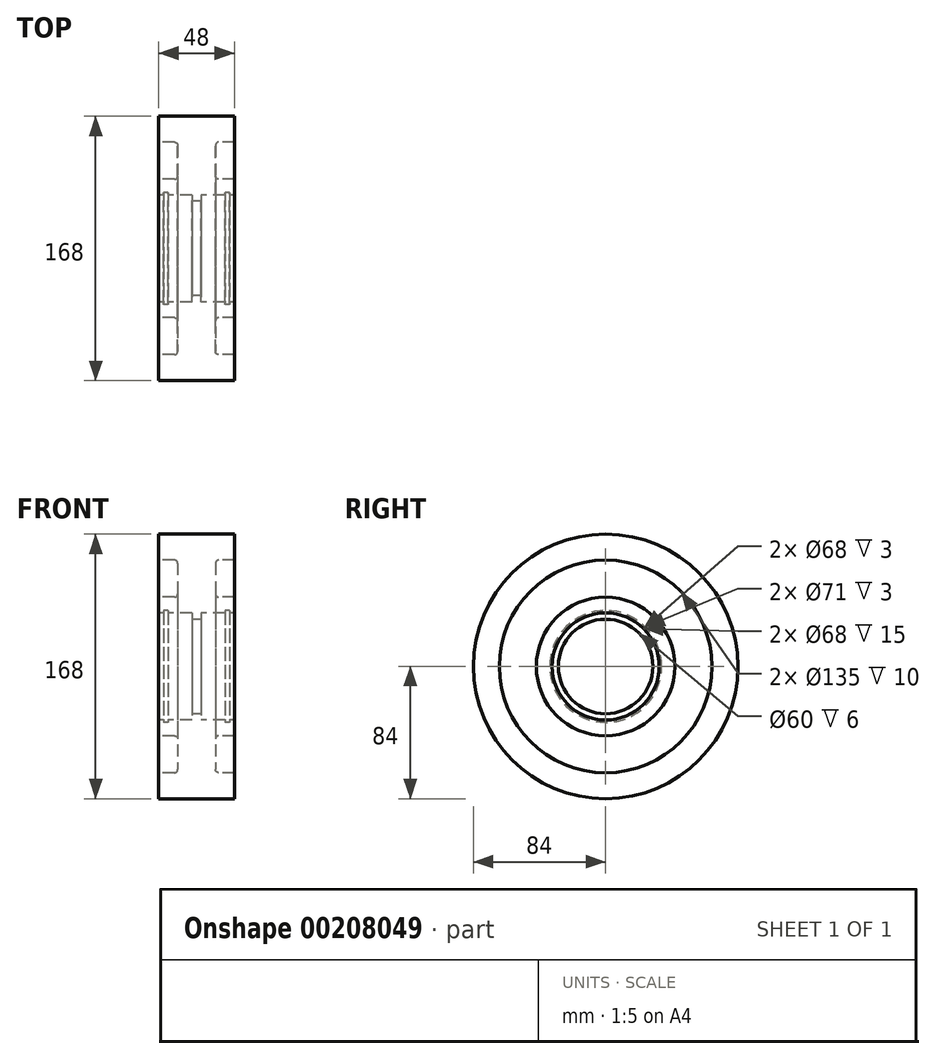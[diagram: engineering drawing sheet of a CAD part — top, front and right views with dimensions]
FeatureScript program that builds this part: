
annotation { "Feature Type Name" : "Feature", "Feature Type Description" : "" }
export const myFeature = defineFeature(function(context is Context, id is Id, definition is map)
    precondition{}
    {
        {
            var Q0;
            Q0=qCreatedBy(makeId("Front.planeOp"),FACE);
            var sketch = newSketch(context, id + "F0", { "sketchPlane" : qUnion([Q0])});
            skLineSegment(sketch, "E0", {"start": v(0, 0) * mm, "end": v(0, 84) * mm, "construction": true});
            skLineSegment(sketch, "E1", {"start": v(0, 84) * mm, "end": v(-24, 84) * mm});
            skLineSegment(sketch, "E2", {"start": v(-24, 84) * mm, "end": v(-24, 67.5) * mm});
            skLineSegment(sketch, "E3", {"start": v(-24, 0) * mm, "end": v(0, 0) * mm, "construction": true});
            skLineSegment(sketch, "E4", {"start": v(-24, 34) * mm, "end": v(-21, 34) * mm});
            skLineSegment(sketch, "E5", {"start": v(-21, 34) * mm, "end": v(-21, 35.5) * mm});
            skLineSegment(sketch, "E6", {"start": v(-21, 35.5) * mm, "end": v(-18, 35.5) * mm});
            skLineSegment(sketch, "E7", {"start": v(-18, 35.5) * mm, "end": v(-18, 34) * mm});
            skLineSegment(sketch, "E8", {"start": v(-18, 34) * mm, "end": v(-3, 34) * mm});
            skLineSegment(sketch, "E9", {"start": v(-3, 34) * mm, "end": v(-3, 30) * mm});
            skLineSegment(sketch, "E10", {"start": v(-3, 30) * mm, "end": v(0, 30) * mm});
            skLineSegment(sketch, "E11", {"start": v(-24, 44) * mm, "end": v(-14, 44) * mm});
            skLineSegment(sketch, "E12", {"start": v(-12, 46) * mm, "end": v(-12, 65.5) * mm});
            skLineSegment(sketch, "E13", {"start": v(-14, 67.5) * mm, "end": v(-24, 67.5) * mm});
            skLineSegment(sketch, "E14.trimOffspring", {"start": v(-24, 44) * mm, "end": v(-24, 34) * mm});
            skPoint(sketch, "E15.visualSharp", {"position": v(-12, 67.5) * mm});
            skArc(sketch, "E15.filletArc", {"start": v(-12, 65.5) * mm, "mid": v(-12.59, 66.91) * mm, "end": v(-14, 67.5) * mm});
            skPoint(sketch, "E16.visualSharp", {"position": v(-12, 44) * mm});
            skArc(sketch, "E16.filletArc", {"start": v(-14, 44) * mm, "mid": v(-12.59, 44.59) * mm, "end": v(-12, 46) * mm});
            skLineSegment(sketch, "E17.MirrorCS", {"start": v(0, 84) * mm, "end": v(24, 84) * mm});
            skLineSegment(sketch, "E18.MirrorCS", {"start": v(24, 84) * mm, "end": v(24, 67.5) * mm});
            skLineSegment(sketch, "E19.MirrorCS", {"start": v(14, 67.5) * mm, "end": v(24, 67.5) * mm});
            skArc(sketch, "E20.MirrorCS", {"start": v(12, 65.5) * mm, "mid": v(12.59, 66.91) * mm, "end": v(14, 67.5) * mm});
            skLineSegment(sketch, "E21.MirrorCS", {"start": v(12, 46) * mm, "end": v(12, 65.5) * mm});
            skArc(sketch, "E22.MirrorCS", {"start": v(14, 44) * mm, "mid": v(12.59, 44.59) * mm, "end": v(12, 46) * mm});
            skLineSegment(sketch, "E23.MirrorCS", {"start": v(24, 44) * mm, "end": v(14, 44) * mm});
            skLineSegment(sketch, "E24.MirrorCS", {"start": v(24, 44) * mm, "end": v(24, 34) * mm});
            skLineSegment(sketch, "E25.MirrorCS", {"start": v(24, 34) * mm, "end": v(21, 34) * mm});
            skLineSegment(sketch, "E26.MirrorCS", {"start": v(21, 34) * mm, "end": v(21, 35.5) * mm});
            skLineSegment(sketch, "E27.MirrorCS", {"start": v(21, 35.5) * mm, "end": v(18, 35.5) * mm});
            skLineSegment(sketch, "E28.MirrorCS", {"start": v(18, 35.5) * mm, "end": v(18, 34) * mm});
            skLineSegment(sketch, "E29.MirrorCS", {"start": v(18, 34) * mm, "end": v(3, 34) * mm});
            skLineSegment(sketch, "E30.MirrorCS", {"start": v(3, 34) * mm, "end": v(3, 30) * mm});
            skLineSegment(sketch, "E31.MirrorCS", {"start": v(3, 30) * mm, "end": v(0, 30) * mm});
            skSolve(sketch);
        }
        {
            var Q0;
            Q0=makeQuery(id+"F0.imprint","IMPRINT",FACE,{"disambiguationData":[TD([[makeQuery(id+"F0.imprint","IMPRINT",EDGE,{"derivedFrom":sQuery(id+"F0.wireOp",EDGE,"E1")}),1.0]])]});
            var Q1;
            Q1=sQuery(id+"F0.wireOp",EDGE,"E3");
            revolve(context, id + "F1", {"entities" : qUnion([Q0]), "axis" : qUnion([Q1]), "revolveType" : RevolveType.FULL});
        }
    });
